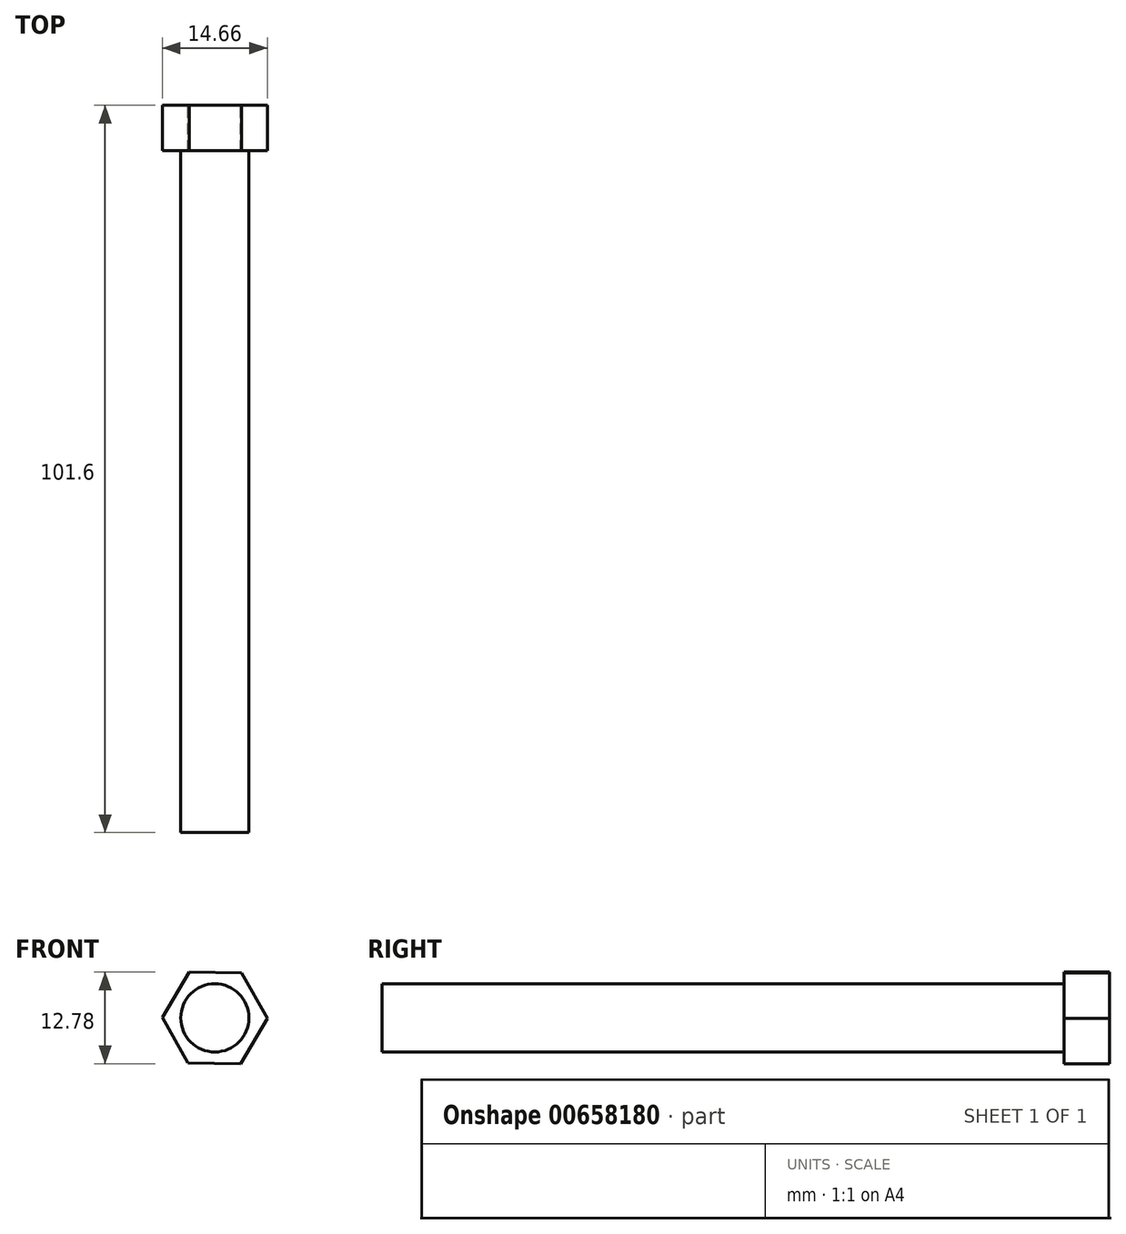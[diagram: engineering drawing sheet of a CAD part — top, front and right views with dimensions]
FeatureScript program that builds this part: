
annotation { "Feature Type Name" : "Feature", "Feature Type Description" : "" }
export const myFeature = defineFeature(function(context is Context, id is Id, definition is map)
    precondition{}
    {
        {
            var Q0;
            Q0=qCreatedBy(makeId("Front.planeOp"),FACE);
            var sketch = newSketch(context, id + "F0", { "sketchPlane" : qUnion([Q0])});
            skCircle(sketch, "E0", {"center": v(0, 0) * mm, "radius": 4.76 * mm});
            skSolve(sketch);
        }
        {
            var Q0;
            Q0 = qSketchRegion(id + "F0", true);
            extrude(context, id + "F1", {"entities" : qUnion([Q0]), "depth" : 101.6 * mm, "offsetDistance" : 25.4 * mm});
        }
        {
            var Q0;
            Q0=qCreatedBy(makeId("Front.planeOp"),FACE);
            var sketch = newSketch(context, id + "F2", { "sketchPlane" : qUnion([Q0])});
            skCircle(sketch, "E1.cCircle", {"center": v(0, 0) * mm, "radius": 6.35 * mm, "construction": true});
            skLineSegment(sketch, "E1.0", {"start": v(3.74, 6.3) * mm, "end": v(7.33, -0.08) * mm});
            skLineSegment(sketch, "E1.1", {"start": v(7.33, -0.08) * mm, "end": v(3.6, -6.4) * mm});
            skLineSegment(sketch, "E1.2", {"start": v(3.6, -6.4) * mm, "end": v(-3.74, -6.3) * mm});
            skLineSegment(sketch, "E1.3", {"start": v(-3.74, -6.3) * mm, "end": v(-7.33, 0.08) * mm});
            skLineSegment(sketch, "E1.4", {"start": v(-7.33, 0.08) * mm, "end": v(-3.6, 6.4) * mm});
            skLineSegment(sketch, "E1.5", {"start": v(-3.6, 6.4) * mm, "end": v(3.74, 6.3) * mm});
            skPoint(sketch, "E1.0.midPoint", {"position": v(5.53, 3.11) * mm});
            skSolve(sketch);
        }
        {
            var Q0;
            Q0=makeQuery(id+"F2.imprint","IMPRINT",FACE,{"disambiguationData":[TD([[makeQuery(id+"F2.imprint","IMPRINT",EDGE,{"derivedFrom":sQuery(id+"F2.wireOp",EDGE,"E1.0")}),-1.0]])]});
            extrude(context, id + "F3", {"entities" : qUnion([Q0]), "operationType" : NewBodyOperationType.ADD, "depth" : 6.35 * mm, "offsetDistance" : 25.4 * mm});
        }
    });
